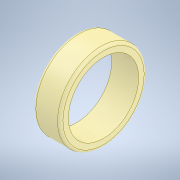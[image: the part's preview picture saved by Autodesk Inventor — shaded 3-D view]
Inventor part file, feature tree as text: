
AUTODESK INVENTOR PART (.ipt)
format: ipt  version: 2022.1 (Build 261234000, 234)  size: 130,048 bytes
history: native  units: mm
features: other x1, extrude x1, fillet x1, sketch x1
ambient origin geometry x8: Origin, YZ Plane, XZ Plane, XY Plane, X Axis, Y Axis, Z Axis, Center Point
bodies: Body1 (feature_tree)
feature tree (4):
  other  "Sólido1"
  extrude  "Extrusión1"  Depth=50.0mm TaperAngle=0.0deg
  fillet  "Empalme1"  Radius=5.0mm
  sketch  "Boceto1"  dims[d0=160.0mm d1=50.0mm d2=0.0mm d3=5.0mm d4=130.0mm]
